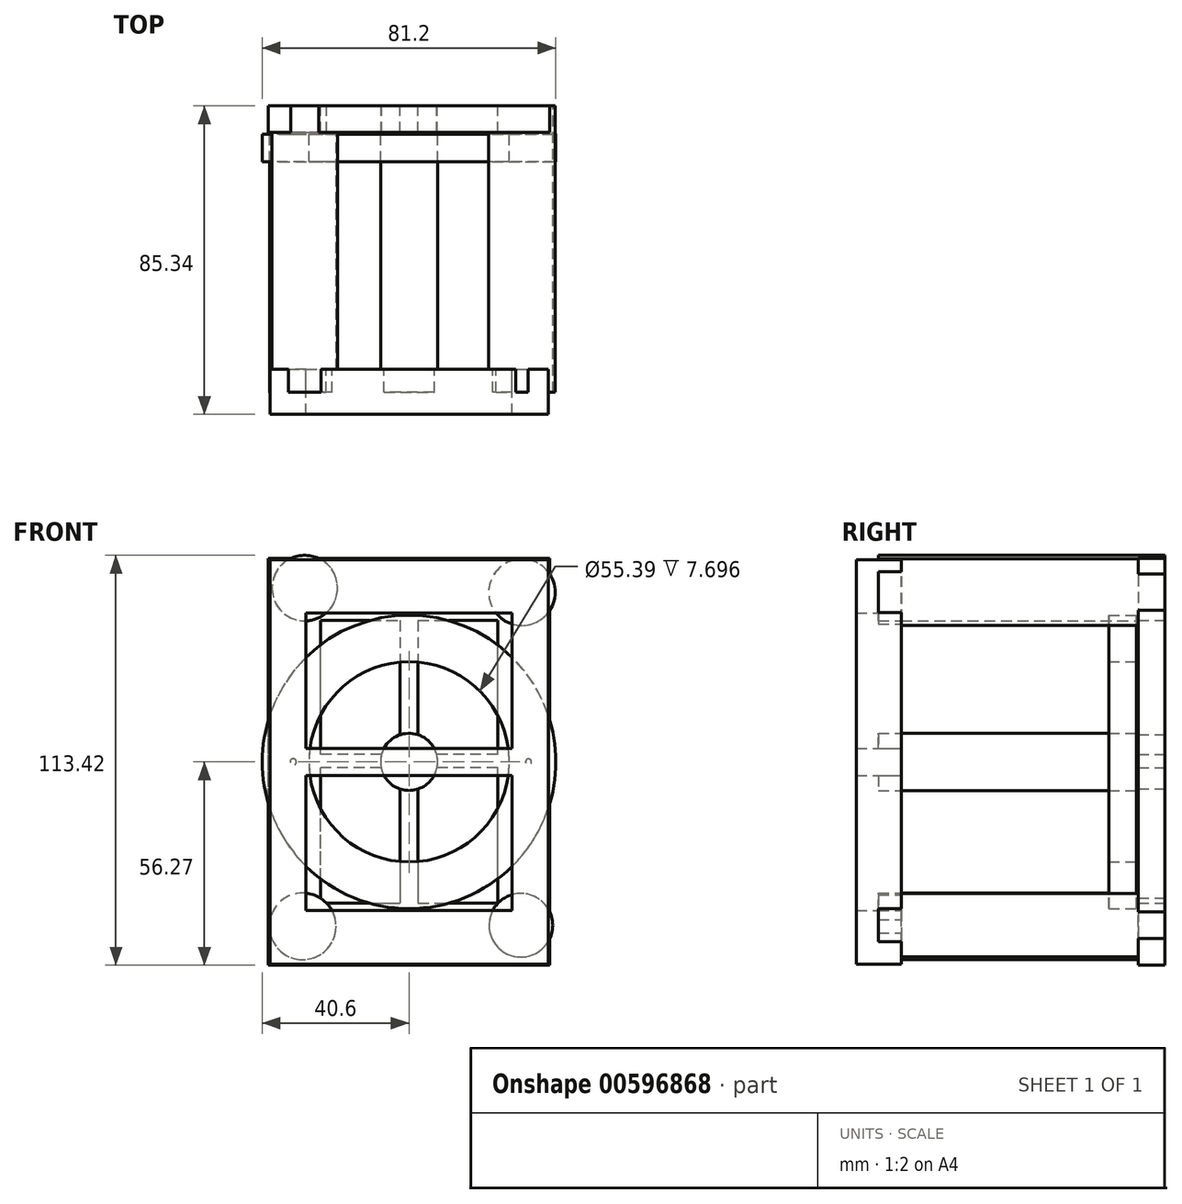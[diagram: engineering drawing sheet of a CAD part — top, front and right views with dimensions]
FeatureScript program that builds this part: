
annotation { "Feature Type Name" : "Feature", "Feature Type Description" : "" }
export const myFeature = defineFeature(function(context is Context, id is Id, definition is map)
    precondition{}
    {
        {
            var Q0;
            Q0=qCreatedBy(makeId("Front.planeOp"),FACE);
            var sketch = newSketch(context, id + "F0", { "sketchPlane" : qUnion([Q0])});
            skLineSegment(sketch, "E0.bottom", {"start": v(-38.91, -56.27) * mm, "end": v(38.91, -56.27) * mm});
            skLineSegment(sketch, "E0.top", {"start": v(-38.91, 56.27) * mm, "end": v(38.91, 56.27) * mm});
            skLineSegment(sketch, "E0.left", {"start": v(-38.91, -56.27) * mm, "end": v(-38.91, 56.27) * mm});
            skLineSegment(sketch, "E0.right", {"start": v(38.91, -56.27) * mm, "end": v(38.91, 56.27) * mm});
            skPoint(sketch, "E0.middle", {"position": v(0, 0) * mm});
            skLineSegment(sketch, "E1.bottom", {"start": v(-24.49, -39.1) * mm, "end": v(24.49, -39.1) * mm});
            skLineSegment(sketch, "E1.top", {"start": v(-24.49, 39.1) * mm, "end": v(24.49, 39.1) * mm});
            skLineSegment(sketch, "E1.left", {"start": v(-24.49, -39.1) * mm, "end": v(-24.49, 39.1) * mm});
            skLineSegment(sketch, "E1.right", {"start": v(24.49, -39.1) * mm, "end": v(24.49, 39.1) * mm});
            skLineSegment(sketch, "E2", {"start": v(2.46, 39.1) * mm, "end": v(2.46, -39.1) * mm});
            skLineSegment(sketch, "E3", {"start": v(-2.51, 39.1) * mm, "end": v(-2.51, -39.1) * mm});
            skLineSegment(sketch, "E4", {"start": v(24.49, 2.06) * mm, "end": v(2.46, 2.06) * mm});
            skLineSegment(sketch, "E5", {"start": v(24.49, -1.62) * mm, "end": v(2.46, -1.62) * mm});
            skLineSegment(sketch, "E6.trimOffspring", {"start": v(-2.51, 2.06) * mm, "end": v(-24.49, 2.06) * mm});
            skLineSegment(sketch, "E7.trimOffspring", {"start": v(-2.51, -1.62) * mm, "end": v(-24.49, -1.62) * mm});
            skSolve(sketch);
        }
        {
            var Q0;
            Q0=qSketchRegion(id+"F0",true);
            var Q1;
            {var subQ0=sQuery(id+"F0.wireOp",EDGE,"E6.trimOffspring");Q1=makeQuery(id+"F0.imprint","IMPRINT",FACE,{"disambiguationData":[TD([[makeQuery(id+"F0.imprint","IMPRINT",EDGE,{"derivedFrom":subQ0}),1.0]])]});}
            var Q2;
            {var subQ0=sQuery(id+"F0.wireOp",EDGE,"E4");Q2=makeQuery(id+"F0.imprint","IMPRINT",FACE,{"disambiguationData":[TD([[makeQuery(id+"F0.imprint","IMPRINT",EDGE,{"derivedFrom":subQ0}),1.0]])]});}
            var Q3;
            {var subQ0=sQuery(id+"F0.wireOp",EDGE,"E2");var subQ5=sQuery(id+"F0.wireOp",EDGE,"E1.bottom");var subQ6=makeQuery(id+"F0.imprint","INTERSECT",VERTEX,{"derivedFrom":[subQ5,subQ0]});Q3=makeQuery(id+"F0.imprint","IMPRINT",FACE,{"disambiguationData":[TD([[makeQuery(id+"F0.imprint","IMPRINT",EDGE,{"disambiguationData":[TD([[subQ6,1.0]])],"derivedFrom":subQ5}),1.0]])]});}
            extrude(context, id + "F1", {"entities" : qUnion([Q0, Q1, Q2, Q3]), "depth" : 7.37 * mm, "offsetDistance" : 25.4 * mm});
        }
        {
            var Q0;
            Q0=qCreatedBy(makeId("Front.planeOp"),FACE);
            var sketch = newSketch(context, id + "F2", { "sketchPlane" : qUnion([Q0])});
            skCircle(sketch, "E8", {"center": v(0, 0) * mm, "radius": 7.9 * mm});
            skCircle(sketch, "E9", {"center": v(31.22, 46.93) * mm, "radius": 9.2 * mm});
            skCircle(sketch, "E10", {"center": v(-28.85, 48.08) * mm, "radius": 9.06 * mm});
            skCircle(sketch, "E11", {"center": v(30.93, -45.2) * mm, "radius": 8.8 * mm});
            skCircle(sketch, "E12", {"center": v(-29.43, -45.49) * mm, "radius": 9.21 * mm});
            skSolve(sketch);
        }
        {
            var Q0;
            Q0=qSketchRegion(id+"F2",true);
            extrude(context, id + "F3", {"entities" : qUnion([Q0]), "operationType" : NewBodyOperationType.ADD, "depth" : 79.25 * mm, "offsetDistance" : 25.4 * mm});
        }
        {
            var Q0;
            Q0=qCreatedBy(makeId("Front.planeOp"),FACE);
            var sketch = newSketch(context, id + "F4", { "sketchPlane" : qUnion([Q0])});
            skCircle(sketch, "E13", {"center": v(33.04, 0) * mm, "radius": 0.82 * mm});
            skCircle(sketch, "E14", {"center": v(-32.05, 0) * mm, "radius": 0.87 * mm});
            skSolve(sketch);
        }
        {
            var Q0;
            Q0=qSketchRegion(id+"F4",true);
            extrude(context, id + "F5", {"entities" : qUnion([Q0]), "operationType" : NewBodyOperationType.ADD, "depth" : 7.85 * mm, "offsetDistance" : 25.4 * mm});
        }
        {
            var Q0;
            Q0=qCreatedBy(makeId("Front.planeOp"),FACE);
            var sketch = newSketch(context, id + "F6", { "sketchPlane" : qUnion([Q0])});
            skCircle(sketch, "E15", {"center": v(0, 0) * mm, "radius": 40.6 * mm});
            skCircle(sketch, "E16", {"center": v(0, 0) * mm, "radius": 27.7 * mm});
            skSolve(sketch);
        }
        {
            var Q0;
            Q0=qSketchRegion(id+"F6",true);
            extrude(context, id + "F7", {"entities" : qUnion([Q0]), "operationType" : NewBodyOperationType.ADD, "depth" : 15.5 * mm, "offsetDistance" : 25.4 * mm, "hasSecondDirection" : true, "secondDirectionOppositeDirection" : false, "secondDirectionDepth" : 7.8 * mm});
        }
        {
            var Q0;
            Q0=qCreatedBy(makeId("Front.planeOp"),FACE);
            var sketch = newSketch(context, id + "F8", { "sketchPlane" : qUnion([Q0])});
            skLineSegment(sketch, "E17.bottom", {"start": v(-38.45, -55.96) * mm, "end": v(38.45, -55.96) * mm});
            skLineSegment(sketch, "E17.top", {"start": v(-38.45, 55.96) * mm, "end": v(38.45, 55.96) * mm});
            skLineSegment(sketch, "E17.left", {"start": v(-38.45, -55.96) * mm, "end": v(-38.45, 55.96) * mm});
            skLineSegment(sketch, "E17.right", {"start": v(38.45, -55.96) * mm, "end": v(38.45, 55.96) * mm});
            skPoint(sketch, "E17.middle", {"position": v(0, 0) * mm});
            skLineSegment(sketch, "E18.bottom", {"start": v(-28.5, -41.15) * mm, "end": v(28.5, -41.15) * mm});
            skLineSegment(sketch, "E18.top", {"start": v(-28.5, 41.15) * mm, "end": v(28.5, 41.15) * mm});
            skLineSegment(sketch, "E18.left", {"start": v(-28.5, -41.15) * mm, "end": v(-28.5, -3.76) * mm});
            skLineSegment(sketch, "E18.right", {"start": v(28.5, -41.15) * mm, "end": v(28.5, -3.76) * mm});
            skLineSegment(sketch, "E19.bottom", {"start": v(-28.5, -3.76) * mm, "end": v(28.5, -3.76) * mm});
            skLineSegment(sketch, "E19.top", {"start": v(-28.5, 3.76) * mm, "end": v(28.5, 3.76) * mm});
            skPoint(sketch, "E20.orphan", {"position": v(-33.83, 3.76) * mm});
            skPoint(sketch, "E21.orphan", {"position": v(-33.83, -3.76) * mm});
            skLineSegment(sketch, "E22.trimOffspring", {"start": v(-28.5, 3.76) * mm, "end": v(-28.5, 41.15) * mm});
            skLineSegment(sketch, "E23.trimOffspring", {"start": v(28.5, 3.76) * mm, "end": v(28.5, 41.15) * mm});
            skPoint(sketch, "E24.orphan", {"position": v(33.83, 3.76) * mm});
            skPoint(sketch, "E25.orphan", {"position": v(33.83, -3.76) * mm});
            skSolve(sketch);
        }
        {
            var Q0;
            Q0=qSketchRegion(id+"F8",true);
            extrude(context, id + "F9", {"entities" : qUnion([Q0]), "operationType" : NewBodyOperationType.ADD, "depth" : 85.34 * mm, "offsetDistance" : 25.4 * mm, "hasSecondDirection" : true, "secondDirectionOppositeDirection" : false, "secondDirectionDepth" : 72.9 * mm});
        }
    });
